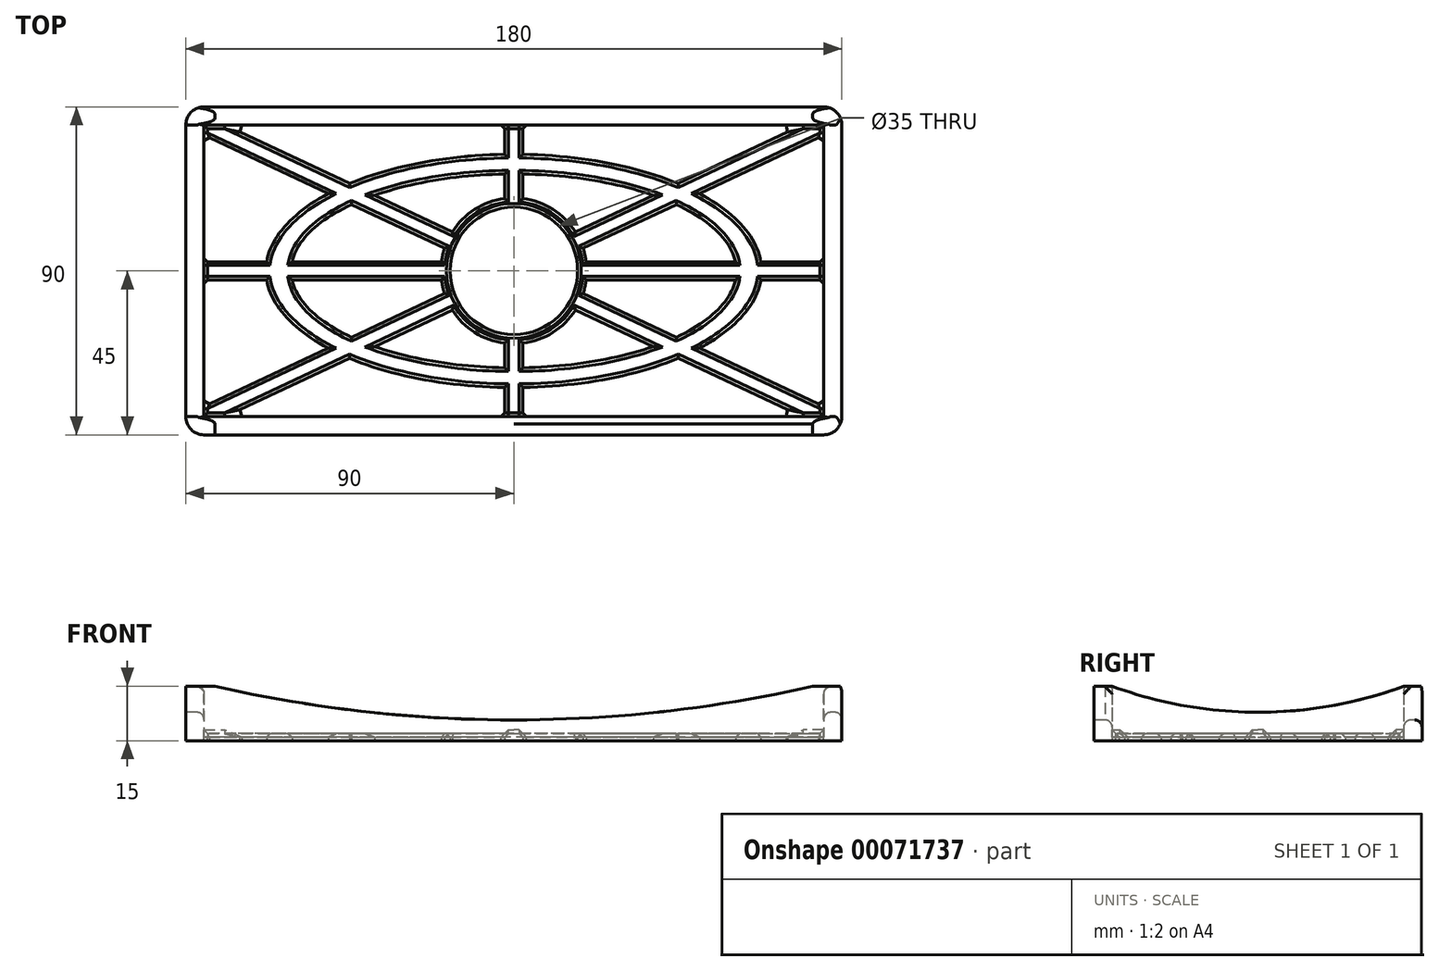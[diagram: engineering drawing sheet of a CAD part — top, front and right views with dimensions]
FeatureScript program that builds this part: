
annotation { "Feature Type Name" : "Feature", "Feature Type Description" : "" }
export const myFeature = defineFeature(function(context is Context, id is Id, definition is map)
    precondition{}
    {
        {
            var Q0;
            Q0=qCreatedBy(makeId("Top.planeOp"),FACE);
            var sketch = newSketch(context, id + "F0", { "sketchPlane" : qUnion([Q0])});
            skLineSegment(sketch, "E0.bottom", {"start": v(0, 45) * mm, "end": v(85, 45) * mm});
            skLineSegment(sketch, "E0.right", {"start": v(90, 40) * mm, "end": v(90, 0) * mm});
            skLineSegment(sketch, "E1.3", {"start": v(85, 40) * mm, "end": v(85, 0) * mm});
            skArc(sketch, "E2.filletArc", {"start": v(90, 40) * mm, "mid": v(88.54, 43.54) * mm, "end": v(85, 45) * mm});
            skArc(sketch, "E3", {"start": v(17.5, 0) * mm, "mid": v(12.37, 12.37) * mm, "end": v(0, 17.5) * mm});
            skLineSegment(sketch, "E4.trimOffspring", {"start": v(16.89, 10.71) * mm, "end": v(38.23, 20.75) * mm});
            skLineSegment(sketch, "E5.trimOffspring", {"start": v(19.02, 6.19) * mm, "end": v(44.56, 18.2) * mm});
            skLineSegment(sketch, "E6", {"start": v(19.84, 2.5) * mm, "end": v(60.83, 2.5) * mm});
            skLineSegment(sketch, "E7", {"start": v(2.5, 40) * mm, "end": v(2.5, 32) * mm});
            skArc(sketch, "E8", {"start": v(19.84, 2.5) * mm, "mid": v(19.52, 4.36) * mm, "end": v(19.02, 6.19) * mm});
            skEllipticalArc(sketch, "E9", {});
            skLineSegment(sketch, "E10.trimOffspring", {"start": v(50.93, 21.2) * mm, "end": v(85, 37.24) * mm});
            skLineSegment(sketch, "E11.trimOffspring", {"start": v(45.06, 23.97) * mm, "end": v(79.13, 40) * mm});
            skEllipticalArc(sketch, "E12.trimOffspring", {});
            skLineSegment(sketch, "E13.trimOffspring", {"start": v(67.77, 2.5) * mm, "end": v(85, 2.5) * mm});
            skArc(sketch, "E14.trimOffspring", {"start": v(16.89, 10.71) * mm, "mid": v(10.72, 16.89) * mm, "end": v(2.5, 19.84) * mm});
            skLineSegment(sketch, "E15.trimOffspring", {"start": v(2.5, 26.58) * mm, "end": v(2.5, 19.84) * mm});
            skLineSegment(sketch, "E16", {"start": v(0, 66.37) * mm, "end": v(0, -116.22) * mm, "construction": true});
            skLineSegment(sketch, "E17.trimOffspring", {"start": v(0, 40) * mm, "end": v(85, 40) * mm});
            skLineSegment(sketch, "E18", {"start": v(-90.57, 0) * mm, "end": v(197.98, 0) * mm, "construction": true});
            skLineSegment(sketch, "E19.MirrorCS", {"start": v(0, 45) * mm, "end": v(-85, 45) * mm});
            skLineSegment(sketch, "E20.MirrorCS", {"start": v(0, 40) * mm, "end": v(-85, 40) * mm});
            skLineSegment(sketch, "E21.MirrorCS", {"start": v(-90, 40) * mm, "end": v(-90, 0) * mm});
            skLineSegment(sketch, "E22.MirrorCS", {"start": v(-85, 40) * mm, "end": v(-85, 0) * mm});
            skLineSegment(sketch, "E23.MirrorCS", {"start": v(-50.93, 21.2) * mm, "end": v(-85, 37.24) * mm});
            skLineSegment(sketch, "E24.MirrorCS", {"start": v(-45.06, 23.97) * mm, "end": v(-79.13, 40) * mm});
            skEllipticalArc(sketch, "E25.MirrorCS", {});
            skArc(sketch, "E26.MirrorCS", {"start": v(-16.89, 10.71) * mm, "mid": v(-10.72, 16.89) * mm, "end": v(-2.5, 19.84) * mm});
            skLineSegment(sketch, "E27.MirrorCS", {"start": v(-2.5, 26.58) * mm, "end": v(-2.5, 19.84) * mm});
            skArc(sketch, "E28.MirrorCS", {"start": v(-17.5, 0) * mm, "mid": v(-12.37, 12.37) * mm, "end": v(0, 17.5) * mm});
            skLineSegment(sketch, "E29.MirrorCS", {"start": v(-16.89, 10.71) * mm, "end": v(-38.23, 20.75) * mm});
            skLineSegment(sketch, "E30.MirrorCS", {"start": v(-19.02, 6.19) * mm, "end": v(-44.56, 18.2) * mm});
            skLineSegment(sketch, "E31.MirrorCS", {"start": v(-19.84, 2.5) * mm, "end": v(-60.83, 2.5) * mm});
            skEllipticalArc(sketch, "E32.MirrorCS", {});
            skArc(sketch, "E33.MirrorCS", {"start": v(-90, 40) * mm, "mid": v(-88.54, 43.54) * mm, "end": v(-85, 45) * mm});
            skLineSegment(sketch, "E34.MirrorCS", {"start": v(0, -45) * mm, "end": v(85, -45) * mm});
            skLineSegment(sketch, "E35.MirrorCS", {"start": v(0, -40) * mm, "end": v(85, -40) * mm});
            skEllipticalArc(sketch, "E36.MirrorCS", {});
            skLineSegment(sketch, "E37.MirrorCS", {"start": v(16.89, -10.71) * mm, "end": v(38.23, -20.75) * mm});
            skLineSegment(sketch, "E38.MirrorCS", {"start": v(19.02, -6.19) * mm, "end": v(44.56, -18.2) * mm});
            skEllipticalArc(sketch, "E39.MirrorCS", {});
            skLineSegment(sketch, "E40.MirrorCS", {"start": v(50.93, -21.2) * mm, "end": v(85, -37.24) * mm});
            skLineSegment(sketch, "E41.MirrorCS", {"start": v(45.06, -23.97) * mm, "end": v(79.13, -40) * mm});
            skArc(sketch, "E42.MirrorCS", {"start": v(16.89, -10.71) * mm, "mid": v(10.72, -16.89) * mm, "end": v(2.5, -19.84) * mm});
            skArc(sketch, "E43.MirrorCS", {"start": v(19.84, -2.5) * mm, "mid": v(19.52, -4.36) * mm, "end": v(19.02, -6.19) * mm});
            skLineSegment(sketch, "E44.MirrorCS", {"start": v(19.84, -2.5) * mm, "end": v(60.83, -2.5) * mm});
            skLineSegment(sketch, "E45.MirrorCS", {"start": v(67.77, -2.5) * mm, "end": v(85, -2.5) * mm});
            skLineSegment(sketch, "E46.MirrorCS", {"start": v(90, -40) * mm, "end": v(90, 0) * mm});
            skLineSegment(sketch, "E47.MirrorCS", {"start": v(85, -40) * mm, "end": v(85, 0) * mm});
            skArc(sketch, "E48.MirrorCS", {"start": v(90, -40) * mm, "mid": v(88.54, -43.54) * mm, "end": v(85, -45) * mm});
            skLineSegment(sketch, "E49.MirrorCS", {"start": v(-67.77, 2.5) * mm, "end": v(-85, 2.5) * mm});
            skArc(sketch, "E50.MirrorCS", {"start": v(-19.84, -2.5) * mm, "mid": v(-19.52, -4.36) * mm, "end": v(-19.02, -6.19) * mm});
            skLineSegment(sketch, "E51.MirrorCS", {"start": v(-16.89, -10.71) * mm, "end": v(-38.23, -20.75) * mm});
            skArc(sketch, "E52.MirrorCS", {"start": v(-90, -40) * mm, "mid": v(-88.54, -43.54) * mm, "end": v(-85, -45) * mm});
            skLineSegment(sketch, "E53.MirrorCS", {"start": v(-67.77, -2.5) * mm, "end": v(-85, -2.5) * mm});
            skEllipticalArc(sketch, "E54.MirrorCS", {});
            skLineSegment(sketch, "E55.MirrorCS", {"start": v(-45.06, -23.97) * mm, "end": v(-79.13, -40) * mm});
            skLineSegment(sketch, "E56.MirrorCS", {"start": v(-50.93, -21.2) * mm, "end": v(-85, -37.24) * mm});
            skLineSegment(sketch, "E57.MirrorCS", {"start": v(0, -45) * mm, "end": v(-85, -45) * mm});
            skLineSegment(sketch, "E58.MirrorCS", {"start": v(-85, -40) * mm, "end": v(-85, 0) * mm});
            skArc(sketch, "E59.MirrorCS", {"start": v(-16.89, -10.71) * mm, "mid": v(-10.72, -16.89) * mm, "end": v(-2.5, -19.84) * mm});
            skEllipticalArc(sketch, "E60.MirrorCS", {});
            skLineSegment(sketch, "E61.MirrorCS", {"start": v(0, -40) * mm, "end": v(-85, -40) * mm});
            skLineSegment(sketch, "E62.MirrorCS", {"start": v(-19.84, -2.5) * mm, "end": v(-60.83, -2.5) * mm});
            skLineSegment(sketch, "E63.MirrorCS", {"start": v(-90, -40) * mm, "end": v(-90, 0) * mm});
            skLineSegment(sketch, "E64.MirrorCS", {"start": v(-19.02, -6.19) * mm, "end": v(-44.56, -18.2) * mm});
            skLineSegment(sketch, "E65.MirrorCS", {"start": v(-2.5, 40) * mm, "end": v(-2.5, 32) * mm});
            skLineSegment(sketch, "E66.MirrorCS", {"start": v(2.5, -40) * mm, "end": v(2.5, -32) * mm});
            skLineSegment(sketch, "E67.MirrorCS", {"start": v(-2.5, -40) * mm, "end": v(-2.5, -32) * mm});
            skLineSegment(sketch, "E68.MirrorCS", {"start": v(-2.5, -26.58) * mm, "end": v(-2.5, -19.84) * mm});
            skLineSegment(sketch, "E69.MirrorCS", {"start": v(2.5, -26.58) * mm, "end": v(2.5, -19.84) * mm});
            skEllipticalArc(sketch, "E70", {});
            skPoint(sketch, "E71.orphan", {"position": v(-38.79, 21.01) * mm});
            skPoint(sketch, "E72.orphan", {"position": v(-45.14, 18.48) * mm});
            skEllipticalArc(sketch, "E73.trimOffspring", {});
            skPoint(sketch, "E74.orphan", {"position": v(-62.67, 2.5) * mm});
            skPoint(sketch, "E75.orphan", {"position": v(-62.67, -2.5) * mm});
            skEllipticalArc(sketch, "E76.trimOffspring", {});
            skPoint(sketch, "E77.orphan", {"position": v(-45.14, -18.48) * mm});
            skPoint(sketch, "E78.orphan", {"position": v(-38.79, -21.01) * mm});
            skEllipticalArc(sketch, "E79.trimOffspring", {});
            skPoint(sketch, "E80.orphan", {"position": v(-2.5, -27) * mm});
            skPoint(sketch, "E81.orphan", {"position": v(2.5, -27) * mm});
            skEllipticalArc(sketch, "E82.trimOffspring", {});
            skPoint(sketch, "E83.orphan", {"position": v(38.79, -21.01) * mm});
            skPoint(sketch, "E84.orphan", {"position": v(45.14, -18.48) * mm});
            skEllipticalArc(sketch, "E85.trimOffspring", {});
            skPoint(sketch, "E86.orphan", {"position": v(62.67, 2.5) * mm});
            skPoint(sketch, "E87.orphan", {"position": v(62.67, -2.5) * mm});
            skEllipticalArc(sketch, "E88.trimOffspring", {});
            skPoint(sketch, "E89.orphan", {"position": v(45.14, 18.48) * mm});
            skPoint(sketch, "E90.orphan", {"position": v(38.79, 21.01) * mm});
            skEllipticalArc(sketch, "E91.trimOffspring", {});
            skPoint(sketch, "E92.orphan", {"position": v(2.5, 27) * mm});
            skPoint(sketch, "E93.orphan", {"position": v(-2.5, 27) * mm});
            skArc(sketch, "E94", {"start": v(-19.02, 6.19) * mm, "mid": v(-19.52, 4.36) * mm, "end": v(-19.84, 2.5) * mm});
            skArc(sketch, "E95.MirrorCS", {"start": v(17.5, 0) * mm, "mid": v(12.37, -12.37) * mm, "end": v(0, -17.5) * mm});
            skArc(sketch, "E96.MirrorCS", {"start": v(-17.5, 0) * mm, "mid": v(-12.37, -12.37) * mm, "end": v(0, -17.5) * mm});
            const initialGuessF0  = {"E9": [0, 0, 1, 0, 0.06798014789819717, 0.03201341759199937, 0.8461276627631339, 1.5340126258255768], "E12.trimOffspring": [0, 0, 1, 0, 0.06798014789819717, 0.03201341759199937, 0.07816962685245432, 0.7239546856422838], "E25.MirrorCS": [0, 0, -1, 0, 0.06798014789819717, 0.03201341759199937, 4.749172681354009, 5.437057644419513], "E32.MirrorCS": [0, 2.76312955155289e-10, -1, 0, 0.06798014789819717, 0.03201341759199937, 5.559230621537303, 6.205015680327132], "E36.MirrorCS": [0, -3.730124438400708e-09, 1, -4.118554320123264e-08, 0.06798014789819717, 0.03201341759199937, 4.749172681354009, 5.437057644418353], "E39.MirrorCS": [0, -4.006437387143198e-09, 1, -4.1185543446162e-08, 0.06798014789819717, 0.03201341759199937, 5.559230621537303, 6.205015688984719], "E54.MirrorCS": [0, -3.730124438400708e-09, -1, -4.118554320123264e-08, 0.06798014789819717, 0.03201341759199937, 0.8461276627611749, 1.5340126258255768], "E60.MirrorCS": [0, -4.006437387143198e-09, -1, -4.1185543446162e-08, 0.06798014789819717, 0.03201341759199937, 0.07816961819486767, 0.7239546856422834], "E70": [0, 0, -1, 0, 0.06110486015677452, 0.026604018942122446, 5.529536341479429, 6.189078364775134], "E73.trimOffspring": [0, 0, -1, 0, 0.06110486015677452, 0.026604018942122446, 0.09410717811343615, 0.7536491171475231], "E76.trimOffspring": [0, 0, -1, 0, 0.06110486015677452, 0.026604018942122446, 0.8948233767912848, 1.5298716499916916], "E79.trimOffspring": [0, 0, -1, 0, 0.06110486015677452, 0.026604018942122446, 1.6117209677351312, 2.2467692767985095], "E82.trimOffspring": [0, 0, -1, 0, 0.06110486015677452, 0.026604018942122446, 2.3879435364422705, 3.047485475476357], "E85.trimOffspring": [0, 0, -1, 0, 0.06110486015677452, 0.026604018942122446, 3.235699595994245, 3.8952416192899504], "E88.trimOffspring": [0, 0, -1, 0, 0.06110486015677452, 0.026604018942122446, 4.036415870746964, 4.671464321512969], "E91.trimOffspring": [0, 0, -1, 0, 0.06110486015677452, 0.026604018942122446, 4.75331363925641, 5.388362090022415]};
            skSetInitialGuess(sketch, initialGuessF0);
            skSolve(sketch);
        }
        {
            var Q0;
            Q0=makeQuery(id+"F0.imprint","IMPRINT",FACE,{"disambiguationData":[TD([[makeQuery(id+"F0.imprint","IMPRINT",EDGE,{"derivedFrom":sQuery(id+"F0.wireOp",EDGE,"E0.bottom")}),-1.0]])]});
            extrude(context, id + "F1", {"entities" : qUnion([Q0]), "depth" : 15 * mm});
        }
        {
            var Q0;
            Q0=makeQuery(id+"F0.imprint","IMPRINT",FACE,{"disambiguationData":[TD([[makeQuery(id+"F0.imprint","IMPRINT",EDGE,{"derivedFrom":sQuery(id+"F0.wireOp",EDGE,"E3")}),-1.0]])]});
            extrude(context, id + "F2", {"entities" : qUnion([Q0]), "operationType" : NewBodyOperationType.ADD, "depth" : 2 * mm});
        }
        {
            var Q0;
            Q0=makeQuery(id+"F1.opExtrude","SWEPT_FACE",FACE,{"disambiguationData":[OSD([sQuery(id+"F0.wireOp",EDGE,"E57.MirrorCS")])]});
            var sketch = newSketch(context, id + "F3", { "sketchPlane" : qUnion([Q0])});
            skArc(sketch, "E97", {"start": v(-82, 15) * mm, "mid": v(0, 5.75) * mm, "end": v(82, 15) * mm});
            skLineSegment(sketch, "E98", {"start": v(-82, 15) * mm, "end": v(82, 15) * mm});
            skSolve(sketch);
        }
        {
            var Q0;
            Q0 = qSketchRegion(id + "F3", true);
            extrude(context, id + "F4", {"entities" : qUnion([Q0]), "operationType" : NewBodyOperationType.REMOVE, "endBound" : BoundingType.THROUGH_ALL, "oppositeDirection" : true, "depth" : 25 * mm});
        }
        {
            var Q0;
            Q0=makeQuery(id+"F1.opExtrude","SWEPT_FACE",FACE,{"disambiguationData":[OSD([sQuery(id+"F0.wireOp",EDGE,"E21.MirrorCS")])]});
            var sketch = newSketch(context, id + "F5", { "sketchPlane" : qUnion([Q0])});
            skArc(sketch, "E99", {"start": v(-40, 15) * mm, "mid": v(0, 7.84) * mm, "end": v(40, 15) * mm});
            skLineSegment(sketch, "E100", {"start": v(-40, 15) * mm, "end": v(40, 15) * mm});
            skSolve(sketch);
        }
        {
            var Q0;
            Q0 = qSketchRegion(id + "F5", true);
            extrude(context, id + "F6", {"entities" : qUnion([Q0]), "operationType" : NewBodyOperationType.REMOVE, "endBound" : BoundingType.THROUGH_ALL, "oppositeDirection" : true, "depth" : 25 * mm});
        }
        {
            var Q0;
            Q0=makeQuery(id+"F6.boolean.opBoolean","INTERSECT",EDGE,{"derivedFrom":[makeQuery(id+"F1.opExtrude","SWEPT_FACE",FACE,{"disambiguationData":[OSD([sQuery(id+"F0.wireOp",EDGE,"E1.3")])]}),makeQuery(id+"F6.opExtrude","SWEPT_FACE",FACE,{"disambiguationData":[OSD([sQuery(id+"F5.wireOp",EDGE,"E99")])]})]});
            var Q1;
            Q1=makeQuery(id+"F4.boolean.opBoolean","INTERSECT",EDGE,{"derivedFrom":[makeQuery(id+"F1.opExtrude","SWEPT_FACE",FACE,{"disambiguationData":[OSD([sQuery(id+"F0.wireOp",EDGE,"E17.trimOffspring")])]}),makeQuery(id+"F4.opExtrude","SWEPT_FACE",FACE,{"disambiguationData":[OSD([sQuery(id+"F3.wireOp",EDGE,"E97")])]})]});
            var Q2;
            Q2=makeQuery(id+"F4.boolean.opBoolean","INTERSECT",EDGE,{"derivedFrom":[makeQuery(id+"F1.opExtrude","SWEPT_FACE",FACE,{"disambiguationData":[OSD([sQuery(id+"F0.wireOp",EDGE,"E20.MirrorCS")])]}),makeQuery(id+"F4.opExtrude","SWEPT_FACE",FACE,{"disambiguationData":[OSD([sQuery(id+"F3.wireOp",EDGE,"E97")])]})]});
            var Q3;
            Q3=makeQuery(id+"F6.boolean.opBoolean","INTERSECT",EDGE,{"derivedFrom":[makeQuery(id+"F1.opExtrude","SWEPT_FACE",FACE,{"disambiguationData":[OSD([sQuery(id+"F0.wireOp",EDGE,"E22.MirrorCS")])]}),makeQuery(id+"F6.opExtrude","SWEPT_FACE",FACE,{"disambiguationData":[OSD([sQuery(id+"F5.wireOp",EDGE,"E99")])]})]});
            var Q4;
            Q4=makeQuery(id+"F6.boolean.opBoolean","INTERSECT",EDGE,{"derivedFrom":[makeQuery(id+"F1.opExtrude","SWEPT_FACE",FACE,{"disambiguationData":[OSD([sQuery(id+"F0.wireOp",EDGE,"E58.MirrorCS")])]}),makeQuery(id+"F6.opExtrude","SWEPT_FACE",FACE,{"disambiguationData":[OSD([sQuery(id+"F5.wireOp",EDGE,"E99")])]})]});
            var Q5;
            Q5=makeQuery(id+"F4.boolean.opBoolean","INTERSECT",EDGE,{"derivedFrom":[makeQuery(id+"F1.opExtrude","SWEPT_FACE",FACE,{"disambiguationData":[OSD([sQuery(id+"F0.wireOp",EDGE,"E61.MirrorCS")])]}),makeQuery(id+"F4.opExtrude","SWEPT_FACE",FACE,{"disambiguationData":[OSD([sQuery(id+"F3.wireOp",EDGE,"E97")])]})]});
            var Q6;
            Q6=makeQuery(id+"F4.boolean.opBoolean","INTERSECT",EDGE,{"derivedFrom":[makeQuery(id+"F1.opExtrude","SWEPT_FACE",FACE,{"disambiguationData":[OSD([sQuery(id+"F0.wireOp",EDGE,"E35.MirrorCS")])]}),makeQuery(id+"F4.opExtrude","SWEPT_FACE",FACE,{"disambiguationData":[OSD([sQuery(id+"F3.wireOp",EDGE,"E97")])]})]});
            var Q7;
            Q7=makeQuery(id+"F6.boolean.opBoolean","INTERSECT",EDGE,{"derivedFrom":[makeQuery(id+"F1.opExtrude","SWEPT_FACE",FACE,{"disambiguationData":[OSD([sQuery(id+"F0.wireOp",EDGE,"E47.MirrorCS")])]}),makeQuery(id+"F6.opExtrude","SWEPT_FACE",FACE,{"disambiguationData":[OSD([sQuery(id+"F5.wireOp",EDGE,"E99")])]})]});
            var Q8;
            Q8=makeQuery(id+"F6.boolean.opBoolean","COPY",EDGE,{"disambiguationData":[OD(1.0)],"derivedFrom":makeQuery(id+"F6.opExtrude","CAP_EDGE",EDGE,{"disambiguationData":[OSD([sQuery(id+"F5.wireOp",EDGE,"E99")])],"isStart":true})});
            var Q9;
            Q9=makeQuery(id+"F6.boolean.opBoolean","COPY",EDGE,{"disambiguationData":[OD(0.0)],"derivedFrom":makeQuery(id+"F6.opExtrude","CAP_EDGE",EDGE,{"disambiguationData":[OSD([sQuery(id+"F5.wireOp",EDGE,"E99")])],"isStart":true})});
            var Q10;
            Q10=makeQuery(id+"F6.boolean.opBoolean","INTERSECT",EDGE,{"derivedFrom":[makeQuery(id+"F1.opExtrude","SWEPT_FACE",FACE,{"disambiguationData":[OSD([sQuery(id+"F0.wireOp",EDGE,"E0.right")])]}),makeQuery(id+"F6.opExtrude","SWEPT_FACE",FACE,{"disambiguationData":[OSD([sQuery(id+"F5.wireOp",EDGE,"E99")])]})]});
            var Q11;
            Q11=makeQuery(id+"F6.boolean.opBoolean","INTERSECT",EDGE,{"derivedFrom":[makeQuery(id+"F1.opExtrude","SWEPT_FACE",FACE,{"disambiguationData":[OSD([sQuery(id+"F0.wireOp",EDGE,"E46.MirrorCS")])]}),makeQuery(id+"F6.opExtrude","SWEPT_FACE",FACE,{"disambiguationData":[OSD([sQuery(id+"F5.wireOp",EDGE,"E99")])]})]});
            var Q12;
            Q12=makeQuery(id+"F4.boolean.opBoolean","COPY",EDGE,{"disambiguationData":[OD(1.0)],"derivedFrom":makeQuery(id+"F4.opExtrude","CAP_EDGE",EDGE,{"disambiguationData":[OSD([sQuery(id+"F3.wireOp",EDGE,"E97")])],"isStart":true})});
            var Q13;
            Q13=makeQuery(id+"F4.boolean.opBoolean","COPY",EDGE,{"disambiguationData":[OD(0.0)],"derivedFrom":makeQuery(id+"F4.opExtrude","CAP_EDGE",EDGE,{"disambiguationData":[OSD([sQuery(id+"F3.wireOp",EDGE,"E97")])],"isStart":true})});
            var Q14;
            Q14=makeQuery(id+"F4.boolean.opBoolean","INTERSECT",EDGE,{"derivedFrom":[makeQuery(id+"F1.opExtrude","SWEPT_FACE",FACE,{"disambiguationData":[OSD([sQuery(id+"F0.wireOp",EDGE,"E0.bottom"),sQuery(id+"F0.wireOp",EDGE,"E19.MirrorCS")])]}),makeQuery(id+"F4.opExtrude","SWEPT_FACE",FACE,{"disambiguationData":[OSD([sQuery(id+"F3.wireOp",EDGE,"E97")])]})]});
            fillet(context, id + "F7", {"entities" : qUnion([Q0, Q1, Q2, Q3, Q4, Q5, Q6, Q7, Q8, Q9, Q10, Q11, Q12, Q13, Q14]), "radius" : 2 * mm, "tangentPropagation" : true, "allowEdgeOverflow" : false});
        }
        {
            var Q0;
            Q0=makeQuery(id+"F2.opExtrude","CAP_EDGE",EDGE,{"disambiguationData":[OSD([sQuery(id+"F0.wireOp",EDGE,"E91.trimOffspring")])],"isStart":false});
            var Q1;
            Q1=makeQuery(id+"F2.opExtrude","CAP_EDGE",EDGE,{"disambiguationData":[OSD([sQuery(id+"F0.wireOp",EDGE,"E25.MirrorCS")])],"isStart":false});
            var Q2;
            Q2=makeQuery(id+"F2.opExtrude","CAP_EDGE",EDGE,{"disambiguationData":[OSD([sQuery(id+"F0.wireOp",EDGE,"E70")])],"isStart":false});
            var Q3;
            Q3=makeQuery(id+"F2.opExtrude","CAP_EDGE",EDGE,{"disambiguationData":[OSD([sQuery(id+"F0.wireOp",EDGE,"E32.MirrorCS")])],"isStart":false});
            var Q4;
            Q4=makeQuery(id+"F2.opExtrude","CAP_FACE",FACE,{"disambiguationData":[OSD([sQuery(id+"F0.wireOp",EDGE,"E1.3"),sQuery(id+"F0.wireOp",EDGE,"E3"),sQuery(id+"F0.wireOp",EDGE,"E4.trimOffspring"),sQuery(id+"F0.wireOp",EDGE,"E5.trimOffspring"),sQuery(id+"F0.wireOp",EDGE,"E6"),sQuery(id+"F0.wireOp",EDGE,"E7"),sQuery(id+"F0.wireOp",EDGE,"E8"),sQuery(id+"F0.wireOp",EDGE,"E9"),sQuery(id+"F0.wireOp",EDGE,"E10.trimOffspring"),sQuery(id+"F0.wireOp",EDGE,"E11.trimOffspring"),sQuery(id+"F0.wireOp",EDGE,"E12.trimOffspring"),sQuery(id+"F0.wireOp",EDGE,"E13.trimOffspring"),sQuery(id+"F0.wireOp",EDGE,"E14.trimOffspring"),sQuery(id+"F0.wireOp",EDGE,"E15.trimOffspring"),sQuery(id+"F0.wireOp",EDGE,"E17.trimOffspring"),sQuery(id+"F0.wireOp",EDGE,"E20.MirrorCS"),sQuery(id+"F0.wireOp",EDGE,"E22.MirrorCS"),sQuery(id+"F0.wireOp",EDGE,"E23.MirrorCS"),sQuery(id+"F0.wireOp",EDGE,"E24.MirrorCS"),sQuery(id+"F0.wireOp",EDGE,"E25.MirrorCS"),sQuery(id+"F0.wireOp",EDGE,"E26.MirrorCS"),sQuery(id+"F0.wireOp",EDGE,"E27.MirrorCS"),sQuery(id+"F0.wireOp",EDGE,"E28.MirrorCS"),sQuery(id+"F0.wireOp",EDGE,"E29.MirrorCS"),sQuery(id+"F0.wireOp",EDGE,"E30.MirrorCS"),sQuery(id+"F0.wireOp",EDGE,"E31.MirrorCS"),sQuery(id+"F0.wireOp",EDGE,"E32.MirrorCS"),sQuery(id+"F0.wireOp",EDGE,"E35.MirrorCS"),sQuery(id+"F0.wireOp",EDGE,"E36.MirrorCS"),sQuery(id+"F0.wireOp",EDGE,"E37.MirrorCS"),sQuery(id+"F0.wireOp",EDGE,"E38.MirrorCS"),sQuery(id+"F0.wireOp",EDGE,"E39.MirrorCS"),sQuery(id+"F0.wireOp",EDGE,"E40.MirrorCS"),sQuery(id+"F0.wireOp",EDGE,"E41.MirrorCS"),sQuery(id+"F0.wireOp",EDGE,"E42.MirrorCS"),sQuery(id+"F0.wireOp",EDGE,"E43.MirrorCS"),sQuery(id+"F0.wireOp",EDGE,"E44.MirrorCS"),sQuery(id+"F0.wireOp",EDGE,"E45.MirrorCS"),sQuery(id+"F0.wireOp",EDGE,"E47.MirrorCS"),sQuery(id+"F0.wireOp",EDGE,"E49.MirrorCS"),sQuery(id+"F0.wireOp",EDGE,"E50.MirrorCS"),sQuery(id+"F0.wireOp",EDGE,"E51.MirrorCS"),sQuery(id+"F0.wireOp",EDGE,"E53.MirrorCS"),sQuery(id+"F0.wireOp",EDGE,"E54.MirrorCS"),sQuery(id+"F0.wireOp",EDGE,"E55.MirrorCS"),sQuery(id+"F0.wireOp",EDGE,"E56.MirrorCS"),sQuery(id+"F0.wireOp",EDGE,"E58.MirrorCS"),sQuery(id+"F0.wireOp",EDGE,"E59.MirrorCS"),sQuery(id+"F0.wireOp",EDGE,"E60.MirrorCS"),sQuery(id+"F0.wireOp",EDGE,"E61.MirrorCS"),sQuery(id+"F0.wireOp",EDGE,"E62.MirrorCS"),sQuery(id+"F0.wireOp",EDGE,"E64.MirrorCS"),sQuery(id+"F0.wireOp",EDGE,"E65.MirrorCS"),sQuery(id+"F0.wireOp",EDGE,"E66.MirrorCS"),sQuery(id+"F0.wireOp",EDGE,"E67.MirrorCS"),sQuery(id+"F0.wireOp",EDGE,"E68.MirrorCS"),sQuery(id+"F0.wireOp",EDGE,"E69.MirrorCS"),sQuery(id+"F0.wireOp",EDGE,"E70"),sQuery(id+"F0.wireOp",EDGE,"E73.trimOffspring"),sQuery(id+"F0.wireOp",EDGE,"E76.trimOffspring"),sQuery(id+"F0.wireOp",EDGE,"E79.trimOffspring"),sQuery(id+"F0.wireOp",EDGE,"E82.trimOffspring"),sQuery(id+"F0.wireOp",EDGE,"E85.trimOffspring"),sQuery(id+"F0.wireOp",EDGE,"E88.trimOffspring"),sQuery(id+"F0.wireOp",EDGE,"E91.trimOffspring"),sQuery(id+"F0.wireOp",EDGE,"E94"),sQuery(id+"F0.wireOp",EDGE,"E95.MirrorCS"),sQuery(id+"F0.wireOp",EDGE,"E96.MirrorCS")])],"isStart":false});
            chamfer(context, id + "F8", {"entities" : qUnion([Q0, Q1, Q2, Q3, Q4]), "width" : 1 * mm, "tangentPropagation" : true});
        }
    });
